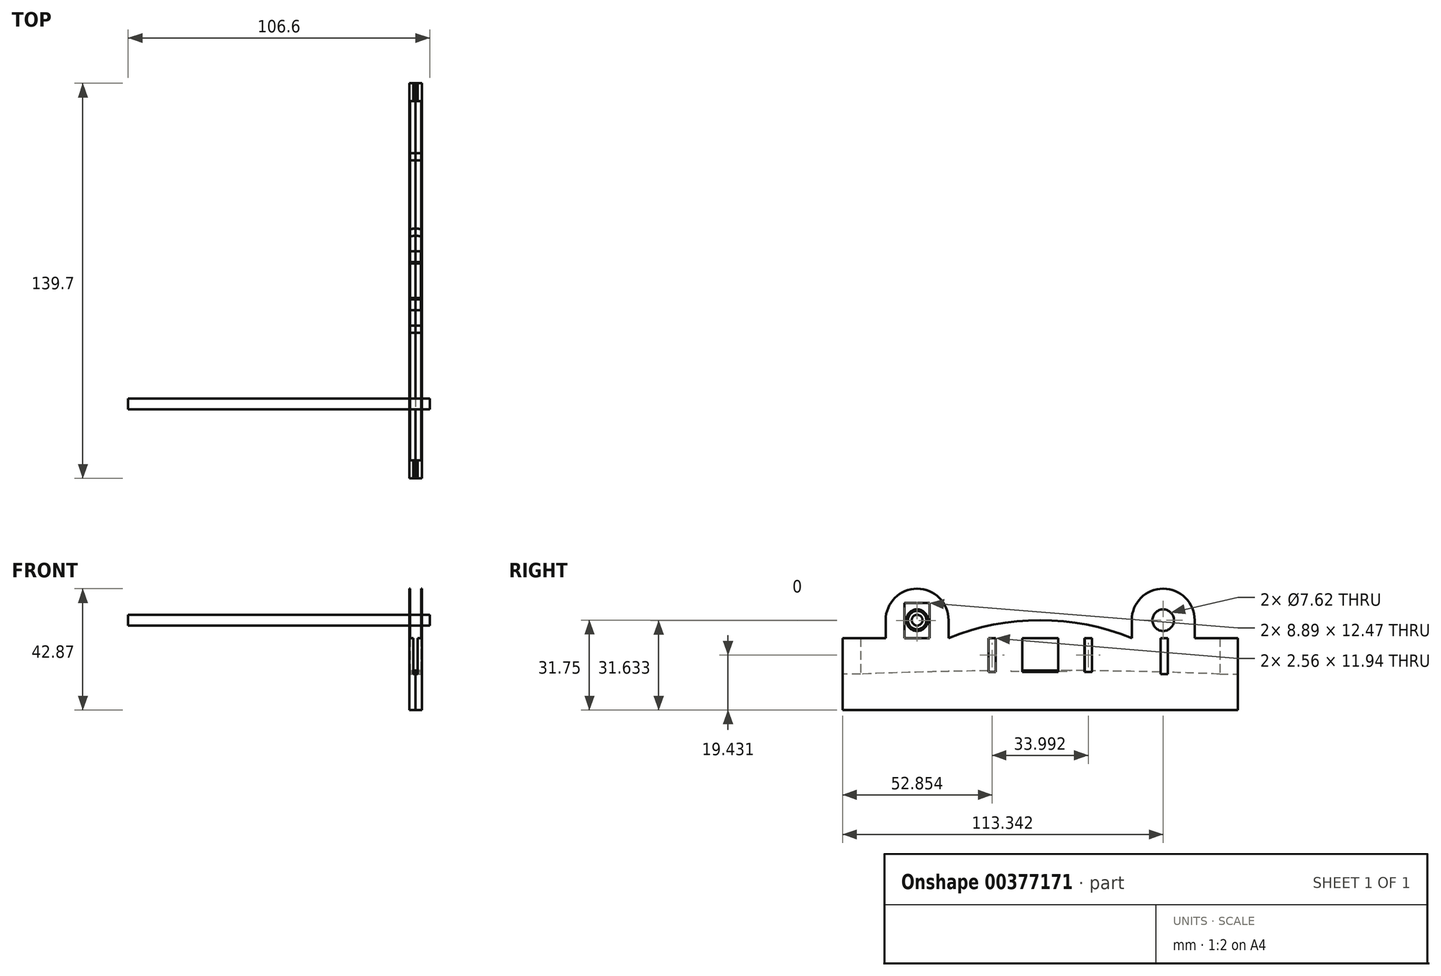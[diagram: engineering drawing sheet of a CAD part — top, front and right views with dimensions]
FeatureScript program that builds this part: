
annotation { "Feature Type Name" : "Feature", "Feature Type Description" : "" }
export const myFeature = defineFeature(function(context is Context, id is Id, definition is map)
    precondition{}
    {
        {
            assignVariable(context, id + "F0", {"name" : "width", "anyValue" : 2.25});
        }
        {
            assignVariable(context, id + "F1", {"name" : "wall", "anyValue" : .25});
        }
        {
            var Q0;
            Q0=qCreatedBy(makeId("Right.planeOp"),FACE);
            var sketch = newSketch(context, id + "F2", { "sketchPlane" : qUnion([Q0])});
            skLineSegment(sketch, "E0", {"start": v(0, 0) * mm, "end": v(69.85, 0) * mm});
            skLineSegment(sketch, "E1", {"start": v(69.85, 0) * mm, "end": v(69.85, 25.4) * mm});
            skLineSegment(sketch, "E2", {"start": v(69.85, 25.4) * mm, "end": v(63.5, 25.4) * mm});
            skLineSegment(sketch, "E3", {"start": v(63.5, 25.4) * mm, "end": v(63.5, 0) * mm});
            skLineSegment(sketch, "E4", {"start": v(32.37, 25.4) * mm, "end": v(63.5, 25.4) * mm});
            skLineSegment(sketch, "E5", {"start": v(0, 0) * mm, "end": v(0, 31.75) * mm, "construction": true});
            skLineSegment(sketch, "E6.MirrorCS", {"start": v(0, 0) * mm, "end": v(-69.85, 0) * mm});
            skLineSegment(sketch, "E7.MirrorCS", {"start": v(-32.37, 25.4) * mm, "end": v(-63.5, 25.4) * mm});
            skLineSegment(sketch, "E8.MirrorCS", {"start": v(-69.85, 25.4) * mm, "end": v(-63.5, 25.4) * mm});
            skLineSegment(sketch, "E9.MirrorCS", {"start": v(-63.5, 25.4) * mm, "end": v(-63.5, 0) * mm});
            skLineSegment(sketch, "E10.MirrorCS", {"start": v(-69.85, 0) * mm, "end": v(-69.85, 25.4) * mm});
            skArc(sketch, "E11", {"start": v(32.37, 25.4) * mm, "mid": v(0, 31.75) * mm, "end": v(-32.37, 25.4) * mm});
            skArc(sketch, "E12", {"start": v(63.5, 12.7) * mm, "mid": v(0, 13.97) * mm, "end": v(-63.5, 12.7) * mm});
            skLineSegment(sketch, "E13", {"start": v(-63.5, 12.7) * mm, "end": v(-69.85, 12.7) * mm});
            skPoint(sketch, "E13.endSnap0", {"position": v(-69.85, 12.7) * mm});
            skLineSegment(sketch, "E14", {"start": v(-69.85, 12.7) * mm, "end": v(-69.85, 0) * mm});
            skLineSegment(sketch, "E15", {"start": v(-63.5, 0) * mm, "end": v(-69.85, 0) * mm});
            skLineSegment(sketch, "E16.MirrorCS", {"start": v(63.5, 12.7) * mm, "end": v(69.85, 12.7) * mm});
            skLineSegment(sketch, "E17.MirrorCS", {"start": v(63.5, 0) * mm, "end": v(69.85, 0) * mm});
            skLineSegment(sketch, "E18.MirrorCS", {"start": v(69.85, 12.7) * mm, "end": v(69.85, 0) * mm});
            skLineSegment(sketch, "E19", {"start": v(32.37, 25.4) * mm, "end": v(32.37, 31.75) * mm});
            skLineSegment(sketch, "E20", {"start": v(54.6, 25.4) * mm, "end": v(54.6, 31.75) * mm});
            skArc(sketch, "E21", {"start": v(54.6, 31.75) * mm, "mid": v(43.5, 42.87) * mm, "end": v(32.37, 31.75) * mm});
            skLineSegment(sketch, "E22.MirrorCS", {"start": v(-54.61, 25.4) * mm, "end": v(-54.61, 31.75) * mm});
            skLineSegment(sketch, "E23.MirrorCS", {"start": v(-32.37, 25.4) * mm, "end": v(-32.37, 31.75) * mm});
            skArc(sketch, "E24.MirrorCS", {"start": v(-54.6, 31.75) * mm, "mid": v(-43.5, 42.87) * mm, "end": v(-32.37, 31.75) * mm});
            skCircle(sketch, "E25", {"center": v(43.5, 31.75) * mm, "radius": 3.81 * mm});
            skCircle(sketch, "E26.MirrorC", {"center": v(-43.5, 31.75) * mm, "radius": 3.81 * mm});
            skCircle(sketch, "E27", {"center": v(-43.5, 31.75) * mm, "radius": 3.26 * mm});
            skLineSegment(sketch, "E28.bottom", {"start": v(-47.94, 37.87) * mm, "end": v(-39.05, 37.87) * mm});
            skLineSegment(sketch, "E28.top", {"start": v(-47.94, 16.08) * mm, "end": v(-39.05, 16.08) * mm});
            skLineSegment(sketch, "E28.left", {"start": v(-47.94, 37.87) * mm, "end": v(-47.94, 16.08) * mm});
            skLineSegment(sketch, "E28.right", {"start": v(-39.05, 37.87) * mm, "end": v(-39.05, 16.08) * mm});
            skLineSegment(sketch, "E29", {"start": v(-43.5, 37.87) * mm, "end": v(-43.5, 16.08) * mm, "construction": true});
            skCircle(sketch, "E30", {"center": v(-43.5, 31.75) * mm, "radius": 1.9 * mm});
            skSolve(sketch);
        }
        {
            var Q0;
            {var subQ7=sQuery(id+"F2.wireOp",EDGE,"E12");Q0=makeQuery(id+"F2.imprint","IMPRINT",FACE,{"disambiguationData":[TD([[makeQuery(id+"F2.imprint","IMPRINT",EDGE,{"derivedFrom":subQ7}),1.0]])]});}
            var Q1;
            {var subQ2=sQuery(id+"F2.wireOp",EDGE,"E13");Q1=makeQuery(id+"F2.imprint","IMPRINT",FACE,{"disambiguationData":[TD([[makeQuery(id+"F2.imprint","IMPRINT",EDGE,{"derivedFrom":subQ2}),1.0]])]});}
            var Q2;
            {var subQ2=sQuery(id+"F2.wireOp",EDGE,"E16.MirrorCS");Q2=makeQuery(id+"F2.imprint","IMPRINT",FACE,{"disambiguationData":[TD([[makeQuery(id+"F2.imprint","IMPRINT",EDGE,{"derivedFrom":subQ2}),-1.0]])]});}
            extrude(context, id + "F3", {"entities" : qUnion([Q0, Q1, Q2]), "depth" : (getVariable(context, 'width')) * mm});
        }
        {
            var Q0;
            {var subQ0=sQuery(id+"F2.wireOp",EDGE,"E8.MirrorCS");Q0=makeQuery(id+"F2.imprint","IMPRINT",FACE,{"disambiguationData":[TD([[makeQuery(id+"F2.imprint","IMPRINT",EDGE,{"derivedFrom":subQ0}),-1.0]])]});}
            var Q1;
            {var subQ2=sQuery(id+"F2.wireOp",EDGE,"E13");Q1=makeQuery(id+"F2.imprint","IMPRINT",FACE,{"disambiguationData":[TD([[makeQuery(id+"F2.imprint","IMPRINT",EDGE,{"derivedFrom":subQ2}),1.0]])]});}
            var Q2;
            {var subQ2=sQuery(id+"F2.wireOp",EDGE,"E16.MirrorCS");Q2=makeQuery(id+"F2.imprint","IMPRINT",FACE,{"disambiguationData":[TD([[makeQuery(id+"F2.imprint","IMPRINT",EDGE,{"derivedFrom":subQ2}),-1.0]])]});}
            var Q3;
            Q3=makeQuery(id+"F2.imprint","IMPRINT",FACE,{"disambiguationData":[TD([[makeQuery(id+"F2.imprint","IMPRINT",EDGE,{"derivedFrom":sQuery(id+"F2.wireOp",EDGE,"E1")}),1.0]])]});
            extrude(context, id + "F4", {"entities" : qUnion([Q0, Q1, Q2, Q3]), "operationType" : NewBodyOperationType.ADD, "depth" : (getVariable(context, 'width')) * mm, "hasSecondDirection" : true, "secondDirectionOppositeDirection" : false, "secondDirectionDepth" : (getVariable(context, 'width') - 1.5) * mm});
        }
        {
            var Q0;
            {var subQ1=sQuery(id+"F2.wireOp",EDGE,"E4");Q0=makeQuery(id+"F2.imprint","IMPRINT",FACE,{"disambiguationData":[TD([[makeQuery(id+"F2.imprint","IMPRINT",EDGE,{"derivedFrom":subQ1}),-1.0]])]});}
            var Q1;
            Q1=makeQuery(id+"F2.imprint","IMPRINT",FACE,{"disambiguationData":[TD([[makeQuery(id+"F2.imprint","IMPRINT",EDGE,{"derivedFrom":sQuery(id+"F2.wireOp",EDGE,"2Wgj5H87-8mqL-qtfe-P2r8-fFbsrGG2HfvN")}),-1.0]])]});
            var Q2;
            {var subQ5=sQuery(id+"F2.wireOp",EDGE,"b9K1u7CE-eBuE-0Knk-ia6g-DoV4v4SQ34Ss.top");Q2=makeQuery(id+"F2.imprint","IMPRINT",FACE,{"disambiguationData":[TD([[makeQuery(id+"F2.imprint","IMPRINT",EDGE,{"derivedFrom":subQ5}),1.0]])]});}
            var Q3;
            {var subQ0=sQuery(id+"F2.wireOp",EDGE,"d7f9dc89-ea1a-419d-968a-98713f555eb78.MirrorCS");Q3=makeQuery(id+"F2.imprint","IMPRINT",FACE,{"disambiguationData":[TD([[makeQuery(id+"F2.imprint","IMPRINT",EDGE,{"derivedFrom":subQ0}),1.0]])]});}
            var Q4;
            Q4=makeQuery(id+"F2.imprint","IMPRINT",FACE,{"disambiguationData":[TD([[makeQuery(id+"F2.imprint","IMPRINT",EDGE,{"derivedFrom":sQuery(id+"F2.wireOp",EDGE,"d7f9dc89-ea1a-419d-968a-98713f555eb71.MirrorC")}),1.0]])]});
            var Q5;
            {var subQ0=sQuery(id+"F2.wireOp",EDGE,"d7f9dc89-ea1a-419d-968a-98713f555eb72.MirrorCS");Q5=makeQuery(id+"F2.imprint","IMPRINT",FACE,{"disambiguationData":[TD([[makeQuery(id+"F2.imprint","IMPRINT",EDGE,{"derivedFrom":subQ0}),-1.0]])]});}
            var Q6;
            {var subQ0=sQuery(id+"F2.wireOp",EDGE,"E19");Q6=makeQuery(id+"F2.imprint","IMPRINT",FACE,{"disambiguationData":[TD([[makeQuery(id+"F2.imprint","IMPRINT",EDGE,{"derivedFrom":subQ0}),-1.0]])]});}
            var Q7;
            {var subQ2=sQuery(id+"F2.wireOp",EDGE,"E22.MirrorCS");Q7=makeQuery(id+"F2.imprint","IMPRINT",FACE,{"disambiguationData":[TD([[makeQuery(id+"F2.imprint","IMPRINT",EDGE,{"derivedFrom":subQ2}),-1.0]])]});}
            var Q8;
            {var subQ5=sQuery(id+"F2.wireOp",EDGE,"E28.top");Q8=makeQuery(id+"F2.imprint","IMPRINT",FACE,{"disambiguationData":[TD([[makeQuery(id+"F2.imprint","IMPRINT",EDGE,{"derivedFrom":subQ5}),1.0]])]});}
            var Q9;
            Q9=makeQuery(id+"F2.imprint","IMPRINT",FACE,{"disambiguationData":[TD([[makeQuery(id+"F2.imprint","IMPRINT",EDGE,{"derivedFrom":sQuery(id+"F2.wireOp",EDGE,"E26.MirrorC")}),1.0]])]});
            extrude(context, id + "F5", {"entities" : qUnion([Q0, Q1, Q2, Q3, Q4, Q5, Q6, Q7, Q8, Q9]), "operationType" : NewBodyOperationType.ADD, "depth" : (getVariable(context, 'width')) * mm, "hasSecondDirection" : true, "secondDirectionOppositeDirection" : false, "secondDirectionDepth" : (getVariable(context, 'width') - getVariable(context, 'wall')) * mm});
        }
        {
            var Q0;
            Q0=makeQuery(id+"F3.opExtrude","SWEPT_BODY",BODY,{"disambiguationData":[OSD([sQuery(id+"F2.wireOp",EDGE,"E0"),sQuery(id+"F2.wireOp",EDGE,"E3"),sQuery(id+"F2.wireOp",EDGE,"E6.MirrorCS"),sQuery(id+"F2.wireOp",EDGE,"E9.MirrorCS"),sQuery(id+"F2.wireOp",EDGE,"E12")])]});
            var Q1;
            {var subQ0=sQuery(id+"F2.wireOp",EDGE,"E4");Q1=makeQuery(id+"F2.imprint","IMPRINT",FACE,{"disambiguationData":[TD([[makeQuery(id+"F2.imprint","IMPRINT",EDGE,{"derivedFrom":subQ0}),-1.0]])]});}
            mirror(context, id + "F6", {"operationType" : NewBodyOperationType.ADD, "entities" : qUnion([Q0]), "mirrorPlane" : qUnion([Q1])});
        }
        {
            var Q0;
            Q0=makeQuery(id+"F2.imprint","IMPRINT",FACE,{"disambiguationData":[TD([[makeQuery(id+"F2.imprint","IMPRINT",EDGE,{"derivedFrom":sQuery(id+"F2.wireOp",EDGE,"E30")}),1.0]])]});
            var Q1;
            Q1=sQuery(id+"F2.wireOp",EDGE,"E27");
            extrude(context, id + "F7", {"entities" : qUnion([Q0]), "surfaceEntities" : qUnion([Q1]), "depth" : (getVariable(context, 'width') * 2 + .5) * mm, "hasSecondDirection" : true, "secondDirectionOppositeDirection" : true, "secondDirectionDepth" : 101.6 * mm});
        }
        {
            var Q0;
            Q0=makeQuery(id+"F5.boolean.opBoolean","MERGE",FACE,{"derivedFrom":[makeQuery(id+"F4.opExtrude","SWEPT_FACE",FACE,{"disambiguationData":[OSD([sQuery(id+"F2.wireOp",EDGE,"E8.MirrorCS")])]}),makeQuery(id+"F5.opExtrude","SWEPT_FACE",FACE,{"disambiguationData":[OSD([sQuery(id+"F2.wireOp",EDGE,"E7.MirrorCS")])]})]});
            var sketch = newSketch(context, id + "F8", { "sketchPlane" : qUnion([Q0])});
            skLineSegment(sketch, "E31.0.5", {"start": v(-50.8, -63.5) * mm, "end": v(-19.05, -63.5) * mm, "construction": true});
            skLineSegment(sketch, "E31.0.6", {"start": v(-19.05, -63.5) * mm, "end": v(19.05, -63.5) * mm, "construction": true});
            skLineSegment(sketch, "E31.0.7", {"start": v(19.05, -63.5) * mm, "end": v(50.8, -63.5) * mm, "construction": true});
            skLineSegment(sketch, "E32", {"start": v(-50.8, 0) * mm, "end": v(-17.14, 0) * mm, "construction": true});
            skArc(sketch, "E33", {"start": v(-18.37, -1.27) * mm, "mid": v(0, -18.41) * mm, "end": v(18.37, -1.27) * mm});
            skCircle(sketch, "E34", {"center": v(0, 0) * mm, "radius": 15.88 * mm});
            skLineSegment(sketch, "E35.bottom", {"start": v(-18.37, -1.27) * mm, "end": v(-50.8, -1.27) * mm});
            skLineSegment(sketch, "E35.top", {"start": v(-18.37, 1.27) * mm, "end": v(-50.8, 1.27) * mm});
            skLineSegment(sketch, "E35.right", {"start": v(-50.8, -1.27) * mm, "end": v(-50.8, 1.27) * mm});
            skPoint(sketch, "E35.middle", {"position": v(-33.98, 0) * mm});
            skLineSegment(sketch, "E36", {"start": v(0, 0) * mm, "end": v(0, 63.5) * mm, "construction": true});
            skLineSegment(sketch, "E37.MirrorCS", {"start": v(50.8, 0) * mm, "end": v(17.14, 0) * mm, "construction": true});
            skLineSegment(sketch, "E38.MirrorCS", {"start": v(18.37, 1.27) * mm, "end": v(50.8, 1.27) * mm});
            skLineSegment(sketch, "E39.MirrorCS", {"start": v(18.37, -1.27) * mm, "end": v(50.8, -1.27) * mm});
            skArc(sketch, "E40.trimOffspring", {"start": v(18.37, 1.27) * mm, "mid": v(0, 18.41) * mm, "end": v(-18.37, 1.27) * mm});
            skLineSegment(sketch, "E41", {"start": v(50.8, 1.27) * mm, "end": v(50.8, -1.27) * mm});
            skLineSegment(sketch, "E42", {"start": v(-30.48, 63.5) * mm, "end": v(-30.48, 42.55) * mm});
            skLineSegment(sketch, "E43", {"start": v(-30.48, 42.55) * mm, "end": v(0, 42.55) * mm});
            skLineSegment(sketch, "E44", {"start": v(-27.94, 63.5) * mm, "end": v(-27.94, 45.1) * mm});
            skLineSegment(sketch, "E45", {"start": v(-27.94, 45.1) * mm, "end": v(0, 45.1) * mm});
            skLineSegment(sketch, "E46.MirrorCS", {"start": v(30.48, 42.55) * mm, "end": v(0, 42.55) * mm});
            skLineSegment(sketch, "E47.MirrorCS", {"start": v(27.94, 45.1) * mm, "end": v(0, 45.1) * mm});
            skLineSegment(sketch, "E48.MirrorCS", {"start": v(27.94, 63.5) * mm, "end": v(27.94, 45.1) * mm});
            skLineSegment(sketch, "E49.MirrorCS", {"start": v(30.48, 63.5) * mm, "end": v(30.48, 42.55) * mm});
            skLineSegment(sketch, "E50", {"start": v(-30.48, 63.5) * mm, "end": v(-27.94, 63.5) * mm});
            skLineSegment(sketch, "E51", {"start": v(27.94, 63.5) * mm, "end": v(30.48, 63.5) * mm});
            skLineSegment(sketch, "E52.MirrorCS", {"start": v(10.15, 0) * mm, "end": v(43.81, 0) * mm, "construction": true});
            skLineSegment(sketch, "E53.MirrorCS", {"start": v(27.94, -63.5) * mm, "end": v(30.48, -63.5) * mm});
            skLineSegment(sketch, "E54.MirrorCS", {"start": v(-30.48, -63.5) * mm, "end": v(-27.94, -63.5) * mm});
            skLineSegment(sketch, "E55.MirrorCS", {"start": v(-30.48, -42.55) * mm, "end": v(0, -42.55) * mm});
            skLineSegment(sketch, "E56.MirrorCS", {"start": v(30.48, -42.55) * mm, "end": v(0, -42.55) * mm});
            skLineSegment(sketch, "E57.MirrorCS", {"start": v(27.94, -63.5) * mm, "end": v(27.94, -45.1) * mm});
            skLineSegment(sketch, "E58.MirrorCS", {"start": v(30.48, -63.5) * mm, "end": v(30.48, -42.55) * mm});
            skLineSegment(sketch, "E59.MirrorCS", {"start": v(27.94, -45.1) * mm, "end": v(0, -45.1) * mm});
            skLineSegment(sketch, "E60.MirrorCS", {"start": v(-27.94, -45.1) * mm, "end": v(0, -45.1) * mm});
            skLineSegment(sketch, "E61.MirrorCS", {"start": v(-30.48, -63.5) * mm, "end": v(-30.48, -42.55) * mm});
            skLineSegment(sketch, "E62.MirrorCS", {"start": v(-27.94, -63.5) * mm, "end": v(-27.94, -45.1) * mm});
            skLineSegment(sketch, "E63.bottom", {"start": v(6.35, 6.35) * mm, "end": v(-6.35, 6.35) * mm});
            skLineSegment(sketch, "E63.top", {"start": v(6.35, -6.35) * mm, "end": v(-6.35, -6.35) * mm});
            skLineSegment(sketch, "E63.left", {"start": v(6.35, 6.35) * mm, "end": v(6.35, -6.35) * mm});
            skLineSegment(sketch, "E63.right", {"start": v(-6.35, 6.35) * mm, "end": v(-6.35, -6.35) * mm});
            skLineSegment(sketch, "E64.bottom", {"start": v(1.9, 6.6) * mm, "end": v(-1.9, 6.6) * mm});
            skLineSegment(sketch, "E64.top", {"start": v(1.9, 10.41) * mm, "end": v(-1.9, 10.41) * mm});
            skLineSegment(sketch, "E64.left", {"start": v(1.9, 6.6) * mm, "end": v(1.9, 10.41) * mm});
            skLineSegment(sketch, "E64.right", {"start": v(-1.9, 6.6) * mm, "end": v(-1.9, 10.41) * mm});
            skPoint(sketch, "E64.middle", {"position": v(0, 8.5) * mm});
            skLineSegment(sketch, "E65.MirrorCS", {"start": v(1.9, -6.6) * mm, "end": v(-1.9, -6.6) * mm});
            skLineSegment(sketch, "E66.MirrorCS", {"start": v(-1.9, -6.6) * mm, "end": v(-1.9, -10.41) * mm});
            skLineSegment(sketch, "E67.MirrorCS", {"start": v(1.9, -6.6) * mm, "end": v(1.9, -10.41) * mm});
            skLineSegment(sketch, "E68.MirrorCS", {"start": v(1.9, -10.41) * mm, "end": v(-1.9, -10.41) * mm});
            skLineSegment(sketch, "E69.bottom", {"start": v(1.9, 6.1) * mm, "end": v(-1.9, 6.1) * mm});
            skLineSegment(sketch, "E69.top", {"start": v(1.9, -6.1) * mm, "end": v(-1.9, -6.1) * mm});
            skLineSegment(sketch, "E69.left", {"start": v(1.9, 6.1) * mm, "end": v(1.9, -6.1) * mm});
            skLineSegment(sketch, "E69.right", {"start": v(-1.9, 6.1) * mm, "end": v(-1.9, -6.1) * mm});
            skSolve(sketch);
        }
        {
            var Q0;
            Q0=makeQuery(id+"F8.imprint","IMPRINT",FACE,{"disambiguationData":[TD([[makeQuery(id+"F8.imprint","IMPRINT",EDGE,{"derivedFrom":sQuery(id+"F8.wireOp",EDGE,"E33")}),1.0]])]});
            var Q1;
            Q1=makeQuery(id+"F8.imprint","IMPRINT",FACE,{"disambiguationData":[TD([[makeQuery(id+"F8.imprint","IMPRINT",EDGE,{"derivedFrom":sQuery(id+"F8.wireOp",EDGE,"E63.bottom")}),1.0]])]});
            extrude(context, id + "F9", {"entities" : qUnion([Q0, Q1]), "operationType" : NewBodyOperationType.REMOVE, "oppositeDirection" : true, "depth" : 11.94 * mm});
        }
        {
            var Q0;
            Q0=makeQuery(id+"F8.imprint","IMPRINT",FACE,{"disambiguationData":[TD([[makeQuery(id+"F8.imprint","IMPRINT",EDGE,{"derivedFrom":sQuery(id+"F8.wireOp",EDGE,"E65.MirrorCS")}),1.0]])]});
            var Q1;
            Q1=makeQuery(id+"F8.imprint","IMPRINT",FACE,{"disambiguationData":[TD([[makeQuery(id+"F8.imprint","IMPRINT",EDGE,{"derivedFrom":sQuery(id+"F8.wireOp",EDGE,"E64.bottom")}),-1.0]])]});
            extrude(context, id + "F10", {"entities" : qUnion([Q0, Q1]), "operationType" : NewBodyOperationType.REMOVE, "oppositeDirection" : true, "depth" : 11.68 * mm});
        }
        {
            var Q0;
            Q0=makeQuery(id+"F8.imprint","IMPRINT",FACE,{"disambiguationData":[TD([[makeQuery(id+"F8.imprint","IMPRINT",EDGE,{"derivedFrom":sQuery(id+"F8.wireOp",EDGE,"E53.MirrorCS")}),-1.0]])]});
            var Q1;
            Q1=makeQuery(id+"F8.imprint","IMPRINT",FACE,{"disambiguationData":[TD([[makeQuery(id+"F8.imprint","IMPRINT",EDGE,{"derivedFrom":sQuery(id+"F8.wireOp",EDGE,"E42")}),1.0]])]});
            extrude(context, id + "F11", {"entities" : qUnion([Q0, Q1]), "operationType" : NewBodyOperationType.REMOVE, "oppositeDirection" : true, "depth" : 12.7 * mm});
        }
    });
